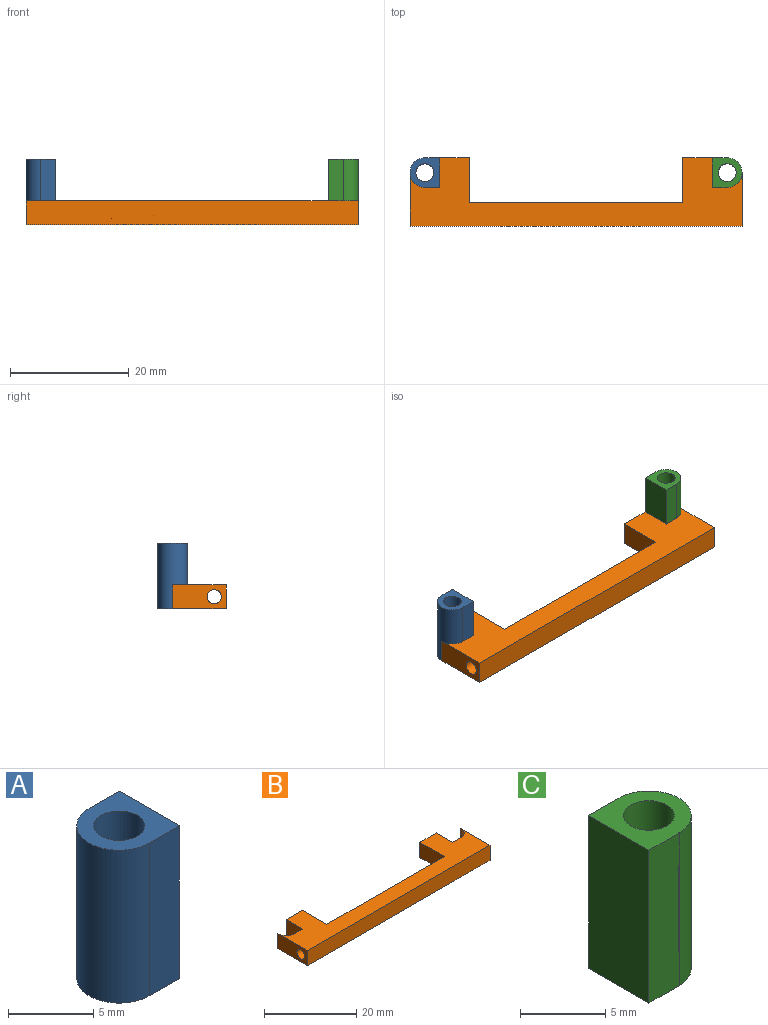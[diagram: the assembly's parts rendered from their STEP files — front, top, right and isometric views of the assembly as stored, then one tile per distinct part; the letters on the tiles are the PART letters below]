
ASSEMBLY  parts=3 mates=2
PART A: 7 faces, bbox 5x5x11 mm
  f0: plane 11x2.5mm, normal (0,1,0), area 27.5mm2, adj f1,f4,f5,f6
  f1: cylinder r=2.5mm len=11mm, axis (0,0,-1), area 86.4mm2, adj f0,f2,f5,f6
  f2: plane 11x2.5mm, normal (0,-1,0), area 27.5mm2, adj f1,f4,f5,f6
  f3: cylinder r=1.5mm len=11mm, axis (0,0,-1), area 103.7mm2, adj f5,f6
  f4: plane 11x5mm, normal (1,0,0), area 55mm2, adj f0,f2,f5,f6
  f5: plane 5x5mm, normal (0,0,1), area 15.2mm2, adj f0,f1,f2,f3,f4
  f6: plane 5x5mm, normal (0,0,-1), area 15.2mm2, adj f0,f1,f2,f3,f4
PART B: 18 faces, bbox 56x11.5x4 mm
  f0: plane 9x4mm, normal (1,0,0), area 31.5mm2, adj f1,f14,f15,f16,f17
  f1: cylinder r=2.5mm len=4mm, axis (0,0,-1), area 15.7mm2, adj f0,f2,f15,f16
  f2: plane 4x0.01mm, normal (-1,0,0), area 0mm2, adj f1,f3,f15,f16
  f3: plane 4x2.5mm, normal (0,1,0), area 10mm2, adj f2,f4,f15,f16
  f4: plane 5.01x4mm, normal (1,0,0), area 20mm2, adj f3,f5,f15,f16
  f5: plane 5x4mm, normal (0,1,0), area 20mm2, adj f4,f6,f15,f16
  f6: plane 7.5x4mm, normal (-1,0,0), area 30mm2, adj f5,f7,f15,f16
  f7: plane 36x4mm, normal (0,1,0), area 144mm2, adj f6,f8,f15,f16
  f8: plane 7.5x4mm, normal (1,0,0), area 30mm2, adj f7,f9,f15,f16
  f9: plane 5x4mm, normal (0,1,0), area 20mm2, adj f8,f10,f15,f16
  f10: plane 5x4mm, normal (-1,0,0), area 20mm2, adj f9,f11,f15,f16
  f11: plane 4x2.5mm, normal (0,1,0), area 10mm2, adj f10,f12,f15,f16
  f12: cylinder r=2.5mm len=4mm, axis (0,0,-1), area 15.7mm2, adj f11,f13,f15,f16
  f13: plane 9x4mm, normal (-1,0,0), area 31.5mm2, adj f12,f14,f15,f16,f17
  f14: plane 56x4mm, normal (0,-1,0), area 224mm2, adj f0,f13,f15,f16
  f15: plane 56x11.5mm, normal (0,0,1), area 326.7mm2, adj f0,f1,f2,f3,f4,f5,f6,f7
  f16: plane 56x11.5mm, normal (0,0,-1), area 326.7mm2, adj f0,f1,f2,f3,f4,f5,f6,f7
  f17: cylinder r=1.2mm len=56mm, axis (-1,0,0), area 422.2mm2, adj f0,f13
PART C: 8 faces, bbox 5x5x11 mm
  f0: cylinder r=2.5mm len=11mm, axis (0,0,-1), area 86.4mm2, adj f1,f5,f6,f7
  f1: plane 11x2.5mm, normal (0,1,0), area 27.5mm2, adj f0,f2,f6,f7
  f2: plane 11x5.01mm, normal (-1,0,0), area 55.1mm2, adj f1,f3,f6,f7
  f3: plane 11x2.5mm, normal (0,-1,0), area 27.5mm2, adj f2,f5,f6,f7
  f4: cylinder r=1.5mm len=11mm, axis (0,0,-1), area 103.7mm2, adj f6,f7
  f5: plane 11x0.01mm, normal (1,0,0), area 0.1mm2, adj f0,f3,f6,f7
  f6: plane 5.01x5mm, normal (0,0,1), area 15.3mm2, adj f0,f1,f2,f3,f4,f5
  f7: plane 5.01x5mm, normal (0,0,-1), area 15.3mm2, adj f0,f1,f2,f3,f4,f5
PLACE A t=(25.36,22.91,4.27)mm
PLACE B t=(25.36,22.91,4.27)mm
PLACE C t=(25.36,22.91,4.27)mm
MATE fastened C.f4 <-> B.f1  axis (0,0,-1) through (76.36,22.91,4.27)mm
MATE fastened B.f12 <-> A.f3  axis (0,0,-1) through (25.36,22.91,4.27)mm
